# Revit family: EKF_EE_СейсмоцокольВСбореTrivia_AVERES
name_source: partatom
category: Электрооборудование
units: mm (PartAtom-declared; Revit-internal decimal feet)

## family parameters
Всегда вертикально = Нет
На основе рабочей плоскости = Да
Общий = Нет
При загрузке вырезать с полостями = Нет
Размер круглого соединителя = Использовать диаметр
Тип детали = Силовой щит
Точка расчета площади = Нет

## types (2) — shared parameters
ADSK_Материал = RAL 7035_Сталь
ADSK_Размер_Высота = 100 мм
ADSK_Размер_Глубина = 610 мм
Глубина = 610 мм
ШиринаУстановкиПереднейЗаднейПанелей = 592 мм
zero-valued in all types: Отметка по умолчанию

## per-type parameters (varying)
| type | ADSK_Размер_Ширина | Передня-Задняя_Панели | Ширина |
| Сейсмоцоколь в сборе Ш600 | 610 мм | EKF_EE_ПередняяЗадняяПанелиСейсмоцоколяTrivia_AVERES : Передняя и задняя панели сейсмоцоколя Ш600 мм EKF AVERES | 610 мм |
| Сейсмоцоколь в сборе Ш800 | 810 мм | EKF_EE_ПередняяЗадняяПанелиСейсмоцоколяTrivia_AVERES : Передняя и задняя панели сейсмоцоколя Ш800 мм EKF AVERES | 810 мм |
